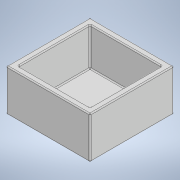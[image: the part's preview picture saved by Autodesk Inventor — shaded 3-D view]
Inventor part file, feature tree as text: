
AUTODESK INVENTOR PART (.ipt)
format: ipt  version: 2022 (Build 260153000, 153)  size: 142,848 bytes
history: native  units: in
note: dims shown in document units (in); Inventor stores cm internally (conversion verified against a paired STEP export)
features: extrude x2, sketch x2, fillet x1
ambient origin geometry x8: Origin, YZ Plane, XZ Plane, XY Plane, X Axis, Y Axis, Z Axis, Center Point
bodies: Solid1 (feature_tree)
feature tree (5):
  extrude  "Extrusion1"  Depth=17.0in
  extrude  "Extrusion2"  Depth=20.0in
  fillet  "Fillet1"  Radius=9.0in
  sketch  "Sketch1"  dims[d0=17.0in d1=17.0in]
  sketch  "Sketch2"  dims[d2=20.0in d3=20.0in d4=9.0in d5=0.0in d6=1.0in d7=0.0in d8=0.25in]
